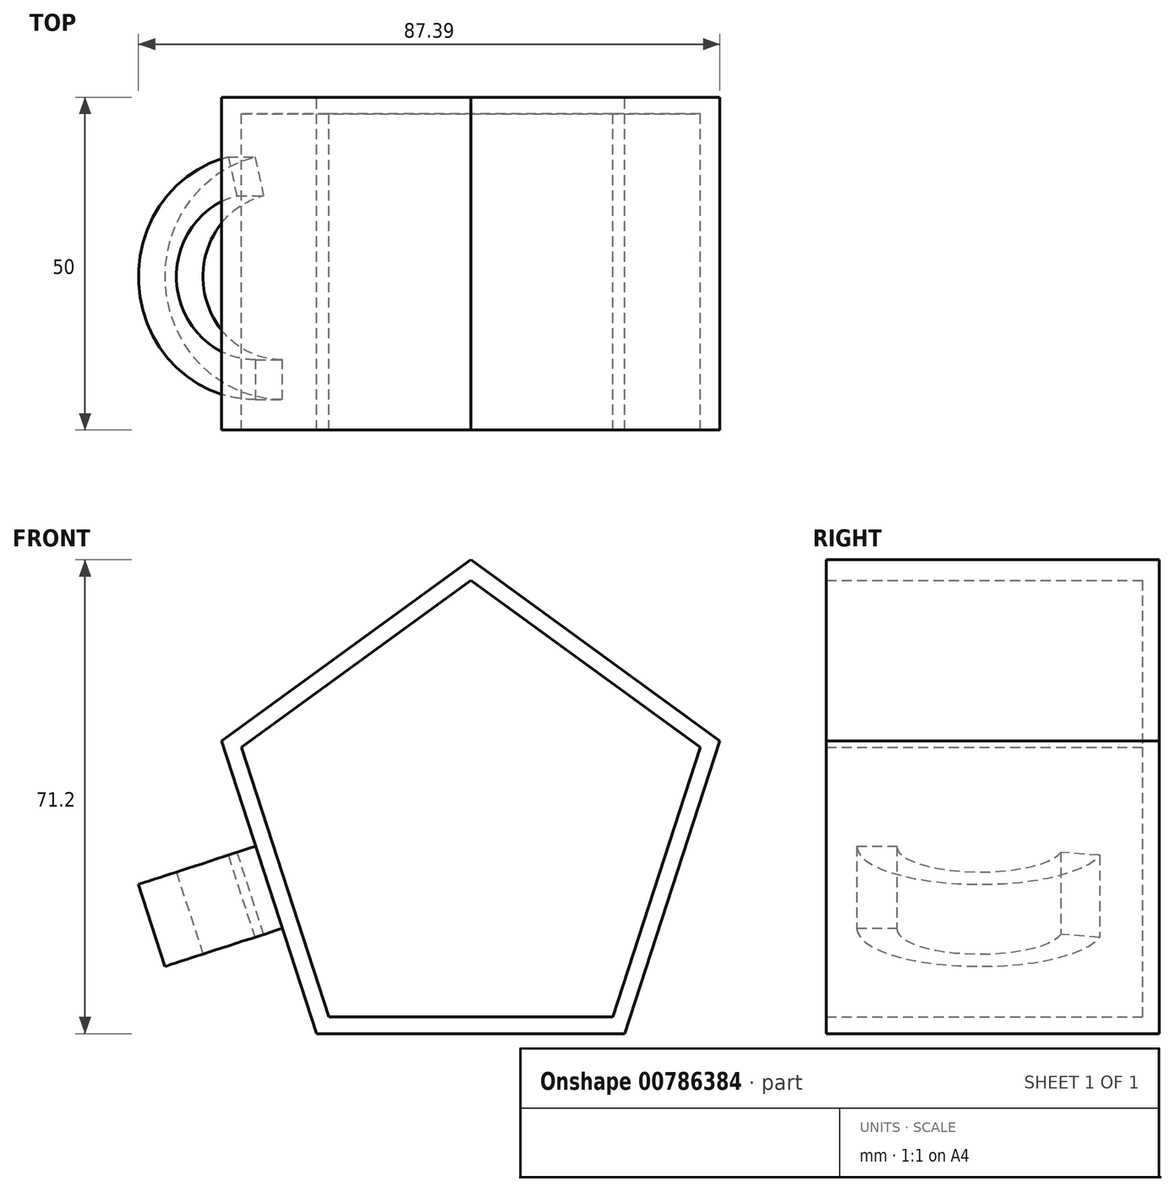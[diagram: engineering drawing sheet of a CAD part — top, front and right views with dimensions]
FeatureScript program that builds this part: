
annotation { "Feature Type Name" : "Feature", "Feature Type Description" : "" }
export const myFeature = defineFeature(function(context is Context, id is Id, definition is map)
    precondition{}
    {
        {
            var Q0;
            Q0=qCreatedBy(makeId("Front.planeOp"),FACE);
            var sketch = newSketch(context, id + "F0", { "sketchPlane" : qUnion([Q0])});
            skLineSegment(sketch, "E0.0", {"start": v(23.14, -31.84) * mm, "end": v(-23.14, -31.84) * mm});
            skLineSegment(sketch, "E0.1", {"start": v(-23.14, -31.84) * mm, "end": v(-37.44, 12.16) * mm});
            skLineSegment(sketch, "E0.2", {"start": v(-37.44, 12.16) * mm, "end": v(0, 39.36) * mm});
            skLineSegment(sketch, "E0.3", {"start": v(0, 39.36) * mm, "end": v(37.44, 12.16) * mm});
            skLineSegment(sketch, "E0.4", {"start": v(37.44, 12.16) * mm, "end": v(23.14, -31.84) * mm});
            skPoint(sketch, "E0.0.midPoint", {"position": v(0, -31.84) * mm});
            skPoint(sketch, "E0.cCircle.center.orphan", {"position": v(0, 0) * mm});
            skSolve(sketch);
        }
        {
            var Q0;
            Q0 = qSketchRegion(id + "F0", true);
            extrude(context, id + "F1", {"entities" : qUnion([Q0]), "depth" : 50 * mm, "offsetDistance" : 25 * mm});
        }
        {
            var Q0;
            Q0=makeQuery(id+"F1.opExtrude","CAP_FACE",FACE,{"disambiguationData":[OSD([sQuery(id+"F0.wireOp",EDGE,"E0.0"),sQuery(id+"F0.wireOp",EDGE,"E0.1"),sQuery(id+"F0.wireOp",EDGE,"E0.2"),sQuery(id+"F0.wireOp",EDGE,"E0.3"),sQuery(id+"F0.wireOp",EDGE,"E0.4")])],"isStart":false});
            shell(context, id + "F2", {"entities" : qUnion([Q0]), "thickness" : 2.5 * mm});
        }
        {
            var Q0;
            Q0=makeQuery(id+"F1.opExtrude","CAP_EDGE",EDGE,{"disambiguationData":[OSD([sQuery(id+"F0.wireOp",EDGE,"E0.1")])],"isStart":true});
            cPoint(context, id + "F3", {"entities" : qUnion([Q0]), "parameter" : 0.5});
        }
        {
            var Q0;
            Q0 = qCreatedBy(id + "F3" ,VERTEX);
            var Q1;
            Q1=makeQuery(id+"F1.opExtrude","CAP_EDGE",EDGE,{"disambiguationData":[OSD([sQuery(id+"F0.wireOp",EDGE,"E0.1")])],"isStart":true});
            cPlane(context, id + "F4", {"entities" : qUnion([Q0, Q1]), "cplaneType" : CPlaneType.LINE_POINT, "offset" : 25 * mm, "width" : 150 * mm, "height" : 150 * mm});
        }
        {
            var Q0;
            Q0=qCreatedBy(id+"F4.planeOp",FACE);
            var sketch = newSketch(context, id + "F5", { "sketchPlane" : qUnion([Q0])});
            skArc(sketch, "E1", {"start": v(-35.04, -41.72) * mm, "mid": v(-32.91, -42.02) * mm, "end": v(-30.76, -42) * mm});
            skArc(sketch, "E2", {"start": v(-30.76, -42) * mm, "mid": v(-16.9, -28.63) * mm, "end": v(-27.44, -12.5) * mm});
            skArc(sketch, "E3", {"start": v(-32.27, -11.83) * mm, "mid": v(-46.97, -25.54) * mm, "end": v(-35.04, -41.72) * mm});
            skArc(sketch, "E4", {"start": v(-27.44, -12.5) * mm, "mid": v(-29.82, -11.97) * mm, "end": v(-32.27, -11.83) * mm});
            skSolve(sketch);
        }
        {
            var Q0;
            Q0=makeQuery(id+"F1.opExtrude","SWEPT_FACE",FACE,{"disambiguationData":[OSD([sQuery(id+"F0.wireOp",EDGE,"E0.1")])]});
            cPlane(context, id + "F6", {"entities" : qUnion([Q0]), "cplaneType" : CPlaneType.OFFSET, "offset" : 0 * mm, "width" : 150 * mm, "height" : 150 * mm});
        }
        {
            var Q0;
            Q0=qCreatedBy(id+"F6.planeOp",FACE);
            var sketch = newSketch(context, id + "F7", { "sketchPlane" : qUnion([Q0])});
            skLineSegment(sketch, "E5.bottom", {"start": v(45.43, 6.48) * mm, "end": v(39.43, 6.48) * mm});
            skLineSegment(sketch, "E5.top", {"start": v(45.43, -6.48) * mm, "end": v(39.43, -6.48) * mm});
            skLineSegment(sketch, "E5.left", {"start": v(45.43, 6.48) * mm, "end": v(45.43, -6.48) * mm});
            skLineSegment(sketch, "E5.right", {"start": v(39.43, 6.48) * mm, "end": v(39.43, -6.48) * mm});
            skPoint(sketch, "E5.middle", {"position": v(42.43, 0) * mm});
            skSolve(sketch);
        }
        {
            var Q0;
            Q0=makeQuery(id+"F7.imprint","IMPRINT",FACE,{"disambiguationData":[TD([[makeQuery(id+"F7.imprint","IMPRINT",EDGE,{"derivedFrom":sQuery(id+"F7.wireOp",EDGE,"E5.bottom")}),1.0]])]});
            var Q1;
            Q1=sQuery(id+"F5.wireOp",EDGE,"E3");
            sweep(context, id + "F8", {"operationType" : NewBodyOperationType.ADD, "profiles" : qUnion([Q0]), "path" : qUnion([Q1])});
        }
    });
